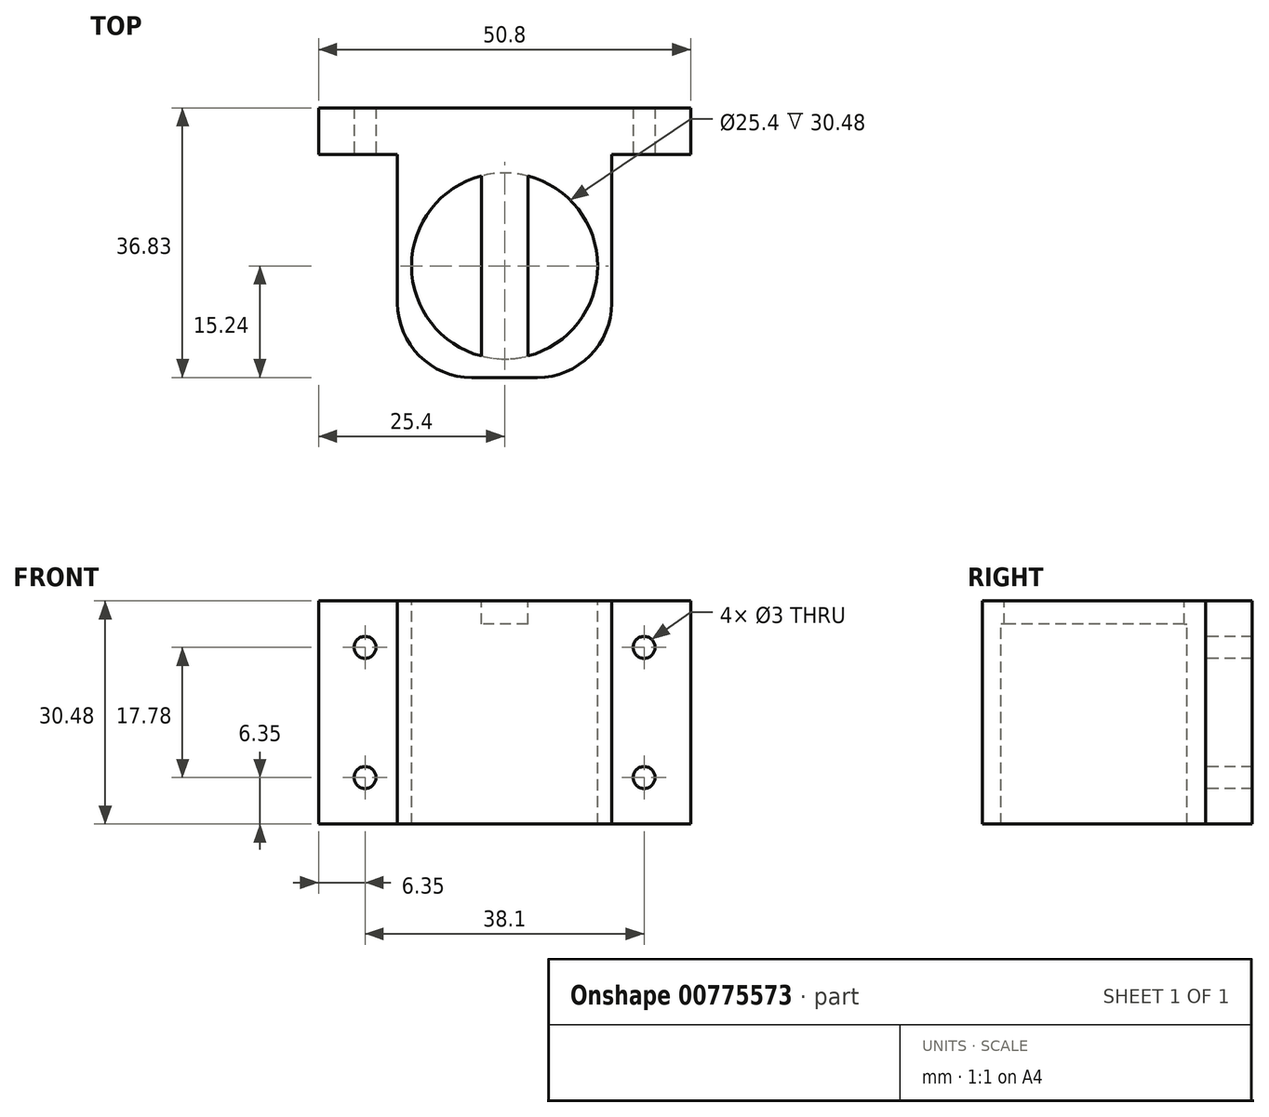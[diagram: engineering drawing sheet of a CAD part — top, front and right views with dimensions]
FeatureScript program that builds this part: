
annotation { "Feature Type Name" : "Feature", "Feature Type Description" : "" }
export const myFeature = defineFeature(function(context is Context, id is Id, definition is map)
    precondition{}
    {
        {
            var Q0;
            Q0=qCreatedBy(makeId("Front.planeOp"),FACE);
            var sketch = newSketch(context, id + "F0", { "sketchPlane" : qUnion([Q0])});
            skLineSegment(sketch, "E0.bottom", {"start": v(25.4, -15.24) * mm, "end": v(-25.4, -15.24) * mm});
            skLineSegment(sketch, "E0.top", {"start": v(25.4, 15.24) * mm, "end": v(-25.4, 15.24) * mm});
            skLineSegment(sketch, "E0.left", {"start": v(25.4, -15.24) * mm, "end": v(25.4, 15.24) * mm});
            skLineSegment(sketch, "E0.right", {"start": v(-25.4, -15.24) * mm, "end": v(-25.4, 15.24) * mm});
            skPoint(sketch, "E0.middle", {"position": v(0, 0) * mm});
            skSolve(sketch);
        }
        {
            var Q0;
            Q0 = qSketchRegion(id + "F0", true);
            extrude(context, id + "F1", {"entities" : qUnion([Q0]), "depth" : 6.35 * mm, "offsetDistance" : 25.4 * mm});
        }
        {
            var Q0;
            Q0=makeQuery(id+"F1.opExtrude","CAP_FACE",FACE,{"disambiguationData":[OSD([sQuery(id+"F0.wireOp",EDGE,"E0.bottom"),sQuery(id+"F0.wireOp",EDGE,"E0.top"),sQuery(id+"F0.wireOp",EDGE,"E0.left"),sQuery(id+"F0.wireOp",EDGE,"E0.right")])],"isStart":false});
            var sketch = newSketch(context, id + "F2", { "sketchPlane" : qUnion([Q0])});
            skCircle(sketch, "E1", {"center": v(-19.05, 8.89) * mm, "radius": 1.5 * mm});
            skCircle(sketch, "E2", {"center": v(-19.05, -8.9) * mm, "radius": 1.5 * mm});
            skCircle(sketch, "E3.MirrorC", {"center": v(19.05, 8.89) * mm, "radius": 1.5 * mm});
            skCircle(sketch, "E4.MirrorC", {"center": v(19.05, -8.9) * mm, "radius": 1.5 * mm});
            skSolve(sketch);
        }
        {
            var Q0;
            Q0 = qSketchRegion(id + "F2", true);
            extrude(context, id + "F3", {"entities" : qUnion([Q0]), "operationType" : NewBodyOperationType.REMOVE, "endBound" : BoundingType.UP_TO_NEXT, "oppositeDirection" : true, "depth" : 25.4 * mm, "offsetDistance" : 25.4 * mm});
        }
        {
            var Q0;
            Q0=makeQuery(id+"F1.opExtrude","CAP_FACE",FACE,{"disambiguationData":[OSD([sQuery(id+"F0.wireOp",EDGE,"E0.bottom"),sQuery(id+"F0.wireOp",EDGE,"E0.top"),sQuery(id+"F0.wireOp",EDGE,"E0.left"),sQuery(id+"F0.wireOp",EDGE,"E0.right")])],"isStart":false});
            var sketch = newSketch(context, id + "F4", { "sketchPlane" : qUnion([Q0])});
            skLineSegment(sketch, "E5.bottom", {"start": v(-14.62, 15.24) * mm, "end": v(14.62, 15.24) * mm});
            skLineSegment(sketch, "E5.top", {"start": v(-14.62, -15.24) * mm, "end": v(14.62, -15.24) * mm});
            skLineSegment(sketch, "E5.left", {"start": v(-14.62, 15.24) * mm, "end": v(-14.62, -15.24) * mm});
            skLineSegment(sketch, "E5.right", {"start": v(14.62, 15.24) * mm, "end": v(14.62, -15.24) * mm});
            skSolve(sketch);
        }
        {
            var Q0;
            Q0 = qSketchRegion(id + "F4", true);
            extrude(context, id + "F5", {"entities" : qUnion([Q0]), "operationType" : NewBodyOperationType.ADD, "depth" : 30.48 * mm, "offsetDistance" : 25.4 * mm});
        }
        {
            var Q0;
            Q0=makeQuery(id+"F5.boolean.opBoolean","MERGE",FACE,{"derivedFrom":[makeQuery(id+"F1.opExtrude","SWEPT_FACE",FACE,{"disambiguationData":[OSD([sQuery(id+"F0.wireOp",EDGE,"E0.top")])]}),makeQuery(id+"F5.opExtrude","SWEPT_FACE",FACE,{"disambiguationData":[OSD([sQuery(id+"F4.wireOp",EDGE,"E5.bottom")])]})]});
            var sketch = newSketch(context, id + "F6", { "sketchPlane" : qUnion([Q0])});
            skLineSegment(sketch, "E6", {"start": v(-14.62, -6.35) * mm, "end": v(14.62, -6.35) * mm});
            skLineSegment(sketch, "E7", {"start": v(0, 0) * mm, "end": v(0, -36.83) * mm});
            skCircle(sketch, "E8", {"center": v(0, -21.59) * mm, "radius": 12.7 * mm});
            skSolve(sketch);
        }
        {
            var Q0;
            Q0 = qSketchRegion(id + "F6", true);
            extrude(context, id + "F7", {"entities" : qUnion([Q0]), "operationType" : NewBodyOperationType.REMOVE, "endBound" : BoundingType.UP_TO_NEXT, "oppositeDirection" : true, "depth" : 25.4 * mm, "offsetDistance" : 25.4 * mm});
        }
        {
            var Q0;
            Q0=makeQuery(id+"F5.opExtrude","CAP_EDGE",EDGE,{"disambiguationData":[OSD([sQuery(id+"F4.wireOp",EDGE,"E5.left")])],"isStart":false});
            var Q1;
            Q1=makeQuery(id+"F5.opExtrude","CAP_EDGE",EDGE,{"disambiguationData":[OSD([sQuery(id+"F4.wireOp",EDGE,"E5.right")])],"isStart":false});
            fillet(context, id + "F8", {"entities" : qUnion([Q0, Q1]), "tangentPropagation" : true, "radius" : 10.16 * mm, "defaultsChanged" : true, "vertexSettings" : [], "allowEdgeOverflow" : false});
        }
        {
            var Q0;
            Q0=makeQuery(id+"F5.boolean.opBoolean","MERGE",FACE,{"derivedFrom":[makeQuery(id+"F1.opExtrude","SWEPT_FACE",FACE,{"disambiguationData":[OSD([sQuery(id+"F0.wireOp",EDGE,"E0.top")])]}),makeQuery(id+"F5.opExtrude","SWEPT_FACE",FACE,{"disambiguationData":[OSD([sQuery(id+"F4.wireOp",EDGE,"E5.bottom")])]})]});
            var sketch = newSketch(context, id + "F9", { "sketchPlane" : qUnion([Q0])});
            skLineSegment(sketch, "E9.bottom", {"start": v(-3.17, 0) * mm, "end": v(3.17, 0) * mm});
            skLineSegment(sketch, "E9.top", {"start": v(-3.18, -36.83) * mm, "end": v(3.18, -36.83) * mm});
            skLineSegment(sketch, "E9.left", {"start": v(-3.17, 0) * mm, "end": v(-3.18, -36.83) * mm});
            skLineSegment(sketch, "E9.right", {"start": v(3.18, 0) * mm, "end": v(3.17, -36.83) * mm});
            skSolve(sketch);
        }
        {
            var Q0;
            Q0 = qSketchRegion(id + "F9", true);
            extrude(context, id + "F10", {"entities" : qUnion([Q0]), "operationType" : NewBodyOperationType.ADD, "oppositeDirection" : true, "depth" : 3.17 * mm, "offsetDistance" : 25.4 * mm});
        }
    });
